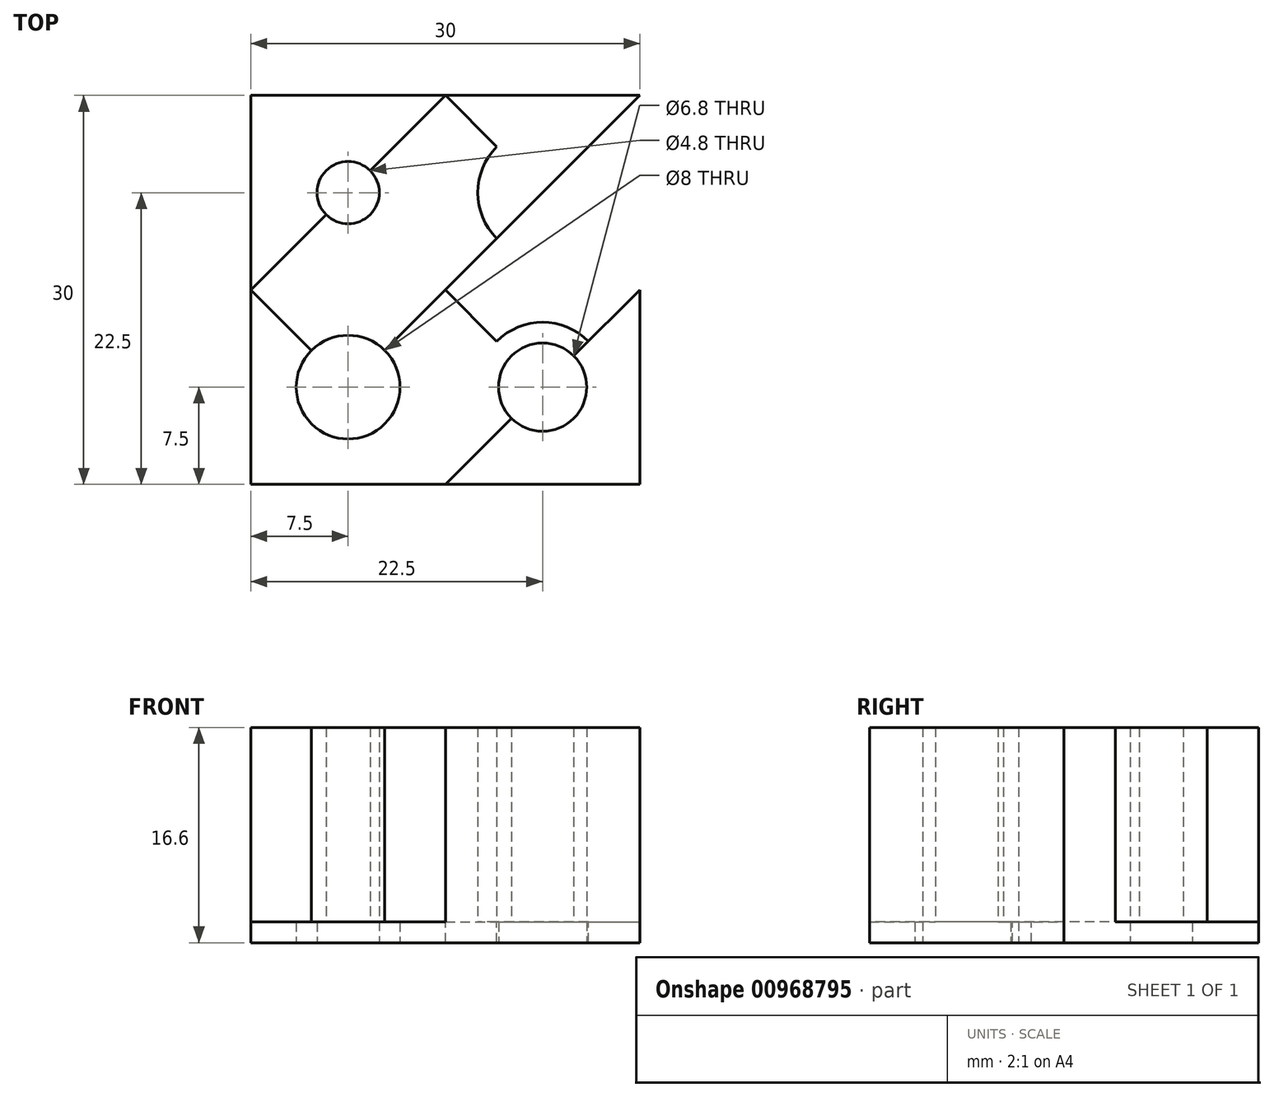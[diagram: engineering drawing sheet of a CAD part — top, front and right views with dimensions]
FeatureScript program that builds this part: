
annotation { "Feature Type Name" : "Feature", "Feature Type Description" : "" }
export const myFeature = defineFeature(function(context is Context, id is Id, definition is map)
    precondition{}
    {
        {
            var Q0;
            Q0=qCreatedBy(makeId("Top.planeOp"),FACE);
            var sketch = newSketch(context, id + "F0", { "sketchPlane" : qUnion([Q0])});
            skLineSegment(sketch, "E0.bottom", {"start": v(0, 0) * mm, "end": v(30, 0) * mm});
            skLineSegment(sketch, "E0.top", {"start": v(0, -30) * mm, "end": v(30, -30) * mm});
            skLineSegment(sketch, "E0.left", {"start": v(0, 0) * mm, "end": v(0, -30) * mm});
            skLineSegment(sketch, "E0.right", {"start": v(30, 0) * mm, "end": v(30, -30) * mm});
            skSolve(sketch);
        }
        {
            var Q0;
            Q0=makeQuery(id+"F0.imprint","IMPRINT",FACE,{"disambiguationData":[TD([[makeQuery(id+"F0.imprint","IMPRINT",EDGE,{"derivedFrom":sQuery(id+"F0.wireOp",EDGE,"E0.bottom")}),-1.0]])]});
            extrude(context, id + "F1", {"entities" : qUnion([Q0]), "depth" : 1.6 * mm, "offsetDistance" : 25 * mm});
        }
        {
            var Q0;
            Q0=makeQuery(id+"F1.opExtrude","CAP_FACE",FACE,{"disambiguationData":[OSD([sQuery(id+"F0.wireOp",EDGE,"E0.bottom"),sQuery(id+"F0.wireOp",EDGE,"E0.top"),sQuery(id+"F0.wireOp",EDGE,"E0.left"),sQuery(id+"F0.wireOp",EDGE,"E0.right")])],"isStart":false});
            var sketch = newSketch(context, id + "F2", { "sketchPlane" : qUnion([Q0])});
            skLineSegment(sketch, "E1", {"start": v(0, 0) * mm, "end": v(30, -30) * mm});
            skLineSegment(sketch, "E2", {"start": v(15, -30) * mm, "end": v(30, -15) * mm});
            skLineSegment(sketch, "E3", {"start": v(15, 0) * mm, "end": v(0, -15) * mm});
            skCircle(sketch, "E4", {"center": v(7.5, -7.5) * mm, "radius": 4 * mm});
            skCircle(sketch, "E5", {"center": v(22.5, -22.5) * mm, "radius": 5 * mm});
            skCircle(sketch, "E6.0", {"center": v(7.5, -7.5) * mm, "radius": 2.4 * mm});
            skLineSegment(sketch, "E7", {"start": v(15, 0) * mm, "end": v(30, -15) * mm});
            skLineSegment(sketch, "E8", {"start": v(0, -15) * mm, "end": v(15, -30) * mm});
            skLineSegment(sketch, "E9", {"start": v(0, -30) * mm, "end": v(30, 0) * mm});
            skCircle(sketch, "E10", {"center": v(22.5, -7.5) * mm, "radius": 5 * mm});
            skCircle(sketch, "E11", {"center": v(7.5, -22.5) * mm, "radius": 4 * mm});
            skCircle(sketch, "E12", {"center": v(22.5, -22.5) * mm, "radius": 3.4 * mm});
            skSolve(sketch);
        }
        {
            var Q0;
            {var subQ0=sQuery(id+"F2.wireOp",EDGE,"E4");var subQ1=sQuery(id+"F2.wireOp",EDGE,"E1");var subQ2=makeQuery(id+"F2.imprint","INTERSECT",VERTEX,{"disambiguationData":[OD(0.0)],"derivedFrom":[subQ1,subQ0]});Q0=makeQuery(id+"F2.imprint","IMPRINT",FACE,{"disambiguationData":[TD([[makeQuery(id+"F2.imprint","IMPRINT",EDGE,{"disambiguationData":[TD([[subQ2,-1.0]])],"derivedFrom":subQ1}),-1.0]])]});}
            var Q1;
            {var subQ0=sQuery(id+"F2.wireOp",EDGE,"E4");var subQ1=sQuery(id+"F2.wireOp",EDGE,"E1");var subQ2=makeQuery(id+"F2.imprint","INTERSECT",VERTEX,{"disambiguationData":[OD(0.0)],"derivedFrom":[subQ1,subQ0]});Q1=makeQuery(id+"F2.imprint","IMPRINT",FACE,{"disambiguationData":[TD([[makeQuery(id+"F2.imprint","IMPRINT",EDGE,{"disambiguationData":[TD([[subQ2,-1.0]])],"derivedFrom":subQ1}),1.0]])]});}
            var Q2;
            {var subQ0=sQuery(id+"F2.wireOp",EDGE,"E6.0");var subQ1=sQuery(id+"F2.wireOp",EDGE,"E1");var subQ2=makeQuery(id+"F2.imprint","INTERSECT",VERTEX,{"disambiguationData":[OD(1.0)],"derivedFrom":[subQ1,subQ0]});Q2=makeQuery(id+"F2.imprint","IMPRINT",FACE,{"disambiguationData":[TD([[makeQuery(id+"F2.imprint","IMPRINT",EDGE,{"disambiguationData":[TD([[subQ2,-1.0]])],"derivedFrom":subQ1}),1.0]])]});}
            var Q3;
            {var subQ0=sQuery(id+"F2.wireOp",EDGE,"E6.0");var subQ1=sQuery(id+"F2.wireOp",EDGE,"E1");var subQ2=makeQuery(id+"F2.imprint","INTERSECT",VERTEX,{"disambiguationData":[OD(1.0)],"derivedFrom":[subQ1,subQ0]});Q3=makeQuery(id+"F2.imprint","IMPRINT",FACE,{"disambiguationData":[TD([[makeQuery(id+"F2.imprint","IMPRINT",EDGE,{"disambiguationData":[TD([[subQ2,-1.0]])],"derivedFrom":subQ1}),-1.0]])]});}
            var Q4;
            {var subQ0=sQuery(id+"F2.wireOp",EDGE,"E5");var subQ1=sQuery(id+"F2.wireOp",EDGE,"E1");var subQ2=makeQuery(id+"F2.imprint","INTERSECT",VERTEX,{"disambiguationData":[OD(0.0)],"derivedFrom":[subQ1,subQ0]});Q4=makeQuery(id+"F2.imprint","IMPRINT",FACE,{"disambiguationData":[TD([[makeQuery(id+"F2.imprint","IMPRINT",EDGE,{"disambiguationData":[TD([[subQ2,-1.0]])],"derivedFrom":subQ1}),-1.0]])]});}
            var Q5;
            {var subQ0=sQuery(id+"F2.wireOp",EDGE,"E5");var subQ1=sQuery(id+"F2.wireOp",EDGE,"E1");var subQ2=makeQuery(id+"F2.imprint","INTERSECT",VERTEX,{"disambiguationData":[OD(0.0)],"derivedFrom":[subQ1,subQ0]});Q5=makeQuery(id+"F2.imprint","IMPRINT",FACE,{"disambiguationData":[TD([[makeQuery(id+"F2.imprint","IMPRINT",EDGE,{"disambiguationData":[TD([[subQ2,-1.0]])],"derivedFrom":subQ1}),1.0]])]});}
            var Q6;
            {var subQ0=sQuery(id+"F2.wireOp",EDGE,"E12");var subQ1=sQuery(id+"F2.wireOp",EDGE,"E1");var subQ2=makeQuery(id+"F2.imprint","INTERSECT",VERTEX,{"disambiguationData":[OD(1.0)],"derivedFrom":[subQ1,subQ0]});Q6=makeQuery(id+"F2.imprint","IMPRINT",FACE,{"disambiguationData":[TD([[makeQuery(id+"F2.imprint","IMPRINT",EDGE,{"disambiguationData":[TD([[subQ2,-1.0]])],"derivedFrom":subQ1}),1.0]])]});}
            var Q7;
            {var subQ0=sQuery(id+"F2.wireOp",EDGE,"E12");var subQ1=sQuery(id+"F2.wireOp",EDGE,"E1");var subQ2=makeQuery(id+"F2.imprint","INTERSECT",VERTEX,{"disambiguationData":[OD(1.0)],"derivedFrom":[subQ1,subQ0]});Q7=makeQuery(id+"F2.imprint","IMPRINT",FACE,{"disambiguationData":[TD([[makeQuery(id+"F2.imprint","IMPRINT",EDGE,{"disambiguationData":[TD([[subQ2,-1.0]])],"derivedFrom":subQ1}),-1.0]])]});}
            extrude(context, id + "F3", {"entities" : qUnion([Q0, Q1, Q2, Q3, Q4, Q5, Q6, Q7]), "operationType" : NewBodyOperationType.ADD, "depth" : 15 * mm, "offsetDistance" : 25 * mm});
        }
        {
            var Q0;
            {var subQ0=sQuery(id+"F2.wireOp",EDGE,"E9");var subQ1=sQuery(id+"F2.wireOp",EDGE,"E7");var subQ2=makeQuery(id+"F2.imprint","INTERSECT",VERTEX,{"derivedFrom":[subQ1,subQ0]});Q0=makeQuery(id+"F2.imprint","IMPRINT",FACE,{"disambiguationData":[TD([[makeQuery(id+"F2.imprint","IMPRINT",EDGE,{"disambiguationData":[TD([[subQ2,-1.0]])],"derivedFrom":subQ1}),-1.0]])]});}
            var Q1;
            {var subQ0=sQuery(id+"F2.wireOp",EDGE,"E10");var subQ1=sQuery(id+"F2.wireOp",EDGE,"E7");var subQ2=makeQuery(id+"F2.imprint","INTERSECT",VERTEX,{"disambiguationData":[OD(0.0)],"derivedFrom":[subQ1,subQ0]});Q1=makeQuery(id+"F2.imprint","IMPRINT",FACE,{"disambiguationData":[TD([[makeQuery(id+"F2.imprint","IMPRINT",EDGE,{"disambiguationData":[TD([[subQ2,-1.0]])],"derivedFrom":subQ1}),-1.0]])]});}
            var Q2;
            {var subQ0=sQuery(id+"F2.wireOp",EDGE,"E10");var subQ1=sQuery(id+"F2.wireOp",EDGE,"E7");var subQ2=makeQuery(id+"F2.imprint","INTERSECT",VERTEX,{"disambiguationData":[OD(0.0)],"derivedFrom":[subQ1,subQ0]});Q2=makeQuery(id+"F2.imprint","IMPRINT",FACE,{"disambiguationData":[TD([[makeQuery(id+"F2.imprint","IMPRINT",EDGE,{"disambiguationData":[TD([[subQ2,-1.0]])],"derivedFrom":subQ1}),1.0]])]});}
            var Q3;
            {var subQ0=sQuery(id+"F2.wireOp",EDGE,"E9");var subQ1=sQuery(id+"F2.wireOp",EDGE,"E7");var subQ2=makeQuery(id+"F2.imprint","INTERSECT",VERTEX,{"derivedFrom":[subQ1,subQ0]});Q3=makeQuery(id+"F2.imprint","IMPRINT",FACE,{"disambiguationData":[TD([[makeQuery(id+"F2.imprint","IMPRINT",EDGE,{"disambiguationData":[TD([[subQ2,-1.0]])],"derivedFrom":subQ1}),1.0]])]});}
            var Q4;
            {var subQ0=sQuery(id+"F2.wireOp",EDGE,"E3");var subQ1=sQuery(id+"F2.wireOp",EDGE,"E1");var subQ2=makeQuery(id+"F2.imprint","INTERSECT",VERTEX,{"derivedFrom":[subQ1,subQ0]});Q4=makeQuery(id+"F2.imprint","IMPRINT",FACE,{"disambiguationData":[TD([[makeQuery(id+"F2.imprint","IMPRINT",EDGE,{"disambiguationData":[TD([[subQ2,-1.0]])],"derivedFrom":subQ1}),1.0]])]});}
            var Q5;
            {var subQ0=sQuery(id+"F2.wireOp",EDGE,"E6.0");var subQ1=sQuery(id+"F2.wireOp",EDGE,"E1");var subQ2=makeQuery(id+"F2.imprint","INTERSECT",VERTEX,{"disambiguationData":[OD(0.0)],"derivedFrom":[subQ1,subQ0]});Q5=makeQuery(id+"F2.imprint","IMPRINT",FACE,{"disambiguationData":[TD([[makeQuery(id+"F2.imprint","IMPRINT",EDGE,{"disambiguationData":[TD([[subQ2,-1.0]])],"derivedFrom":subQ1}),1.0]])]});}
            var Q6;
            {var subQ0=sQuery(id+"F2.wireOp",EDGE,"E6.0");var subQ1=sQuery(id+"F2.wireOp",EDGE,"E1");var subQ2=makeQuery(id+"F2.imprint","INTERSECT",VERTEX,{"disambiguationData":[OD(0.0)],"derivedFrom":[subQ1,subQ0]});Q6=makeQuery(id+"F2.imprint","IMPRINT",FACE,{"disambiguationData":[TD([[makeQuery(id+"F2.imprint","IMPRINT",EDGE,{"disambiguationData":[TD([[subQ2,-1.0]])],"derivedFrom":subQ1}),-1.0]])]});}
            var Q7;
            {var subQ0=sQuery(id+"F2.wireOp",EDGE,"E3");var subQ1=sQuery(id+"F2.wireOp",EDGE,"E1");var subQ2=makeQuery(id+"F2.imprint","INTERSECT",VERTEX,{"derivedFrom":[subQ1,subQ0]});Q7=makeQuery(id+"F2.imprint","IMPRINT",FACE,{"disambiguationData":[TD([[makeQuery(id+"F2.imprint","IMPRINT",EDGE,{"disambiguationData":[TD([[subQ2,-1.0]])],"derivedFrom":subQ1}),-1.0]])]});}
            var Q8;
            {var subQ0=sQuery(id+"F2.wireOp",EDGE,"E11");var subQ1=sQuery(id+"F2.wireOp",EDGE,"E8");var subQ2=makeQuery(id+"F2.imprint","INTERSECT",VERTEX,{"disambiguationData":[OD(0.0)],"derivedFrom":[subQ1,subQ0]});Q8=makeQuery(id+"F2.imprint","IMPRINT",FACE,{"disambiguationData":[TD([[makeQuery(id+"F2.imprint","IMPRINT",EDGE,{"disambiguationData":[TD([[subQ2,-1.0]])],"derivedFrom":subQ1}),1.0]])]});}
            var Q9;
            {var subQ0=sQuery(id+"F2.wireOp",EDGE,"E9");var subQ1=sQuery(id+"F2.wireOp",EDGE,"E8");var subQ2=makeQuery(id+"F2.imprint","INTERSECT",VERTEX,{"derivedFrom":[subQ1,subQ0]});Q9=makeQuery(id+"F2.imprint","IMPRINT",FACE,{"disambiguationData":[TD([[makeQuery(id+"F2.imprint","IMPRINT",EDGE,{"disambiguationData":[TD([[subQ2,-1.0]])],"derivedFrom":subQ1}),1.0]])]});}
            var Q10;
            {var subQ0=sQuery(id+"F2.wireOp",EDGE,"E9");var subQ1=sQuery(id+"F2.wireOp",EDGE,"E8");var subQ2=makeQuery(id+"F2.imprint","INTERSECT",VERTEX,{"derivedFrom":[subQ1,subQ0]});Q10=makeQuery(id+"F2.imprint","IMPRINT",FACE,{"disambiguationData":[TD([[makeQuery(id+"F2.imprint","IMPRINT",EDGE,{"disambiguationData":[TD([[subQ2,-1.0]])],"derivedFrom":subQ1}),-1.0]])]});}
            var Q11;
            {var subQ0=sQuery(id+"F2.wireOp",EDGE,"E11");var subQ1=sQuery(id+"F2.wireOp",EDGE,"E8");var subQ2=makeQuery(id+"F2.imprint","INTERSECT",VERTEX,{"disambiguationData":[OD(0.0)],"derivedFrom":[subQ1,subQ0]});Q11=makeQuery(id+"F2.imprint","IMPRINT",FACE,{"disambiguationData":[TD([[makeQuery(id+"F2.imprint","IMPRINT",EDGE,{"disambiguationData":[TD([[subQ2,-1.0]])],"derivedFrom":subQ1}),-1.0]])]});}
            var Q12;
            {var subQ0=sQuery(id+"F2.wireOp",EDGE,"E12");var subQ1=sQuery(id+"F2.wireOp",EDGE,"E1");var subQ2=makeQuery(id+"F2.imprint","INTERSECT",VERTEX,{"disambiguationData":[OD(0.0)],"derivedFrom":[subQ1,subQ0]});Q12=makeQuery(id+"F2.imprint","IMPRINT",FACE,{"disambiguationData":[TD([[makeQuery(id+"F2.imprint","IMPRINT",EDGE,{"disambiguationData":[TD([[subQ2,-1.0]])],"derivedFrom":subQ1}),-1.0]])]});}
            var Q13;
            {var subQ0=sQuery(id+"F2.wireOp",EDGE,"E12");var subQ1=sQuery(id+"F2.wireOp",EDGE,"E1");var subQ2=makeQuery(id+"F2.imprint","INTERSECT",VERTEX,{"disambiguationData":[OD(0.0)],"derivedFrom":[subQ1,subQ0]});Q13=makeQuery(id+"F2.imprint","IMPRINT",FACE,{"disambiguationData":[TD([[makeQuery(id+"F2.imprint","IMPRINT",EDGE,{"disambiguationData":[TD([[subQ2,-1.0]])],"derivedFrom":subQ1}),1.0]])]});}
            var Q14;
            {var subQ0=sQuery(id+"F2.wireOp",EDGE,"E2");var subQ1=sQuery(id+"F2.wireOp",EDGE,"E1");var subQ2=makeQuery(id+"F2.imprint","INTERSECT",VERTEX,{"derivedFrom":[subQ1,subQ0]});Q14=makeQuery(id+"F2.imprint","IMPRINT",FACE,{"disambiguationData":[TD([[makeQuery(id+"F2.imprint","IMPRINT",EDGE,{"disambiguationData":[TD([[subQ2,-1.0]])],"derivedFrom":subQ1}),1.0]])]});}
            var Q15;
            {var subQ0=sQuery(id+"F2.wireOp",EDGE,"E2");var subQ1=sQuery(id+"F2.wireOp",EDGE,"E1");var subQ2=makeQuery(id+"F2.imprint","INTERSECT",VERTEX,{"derivedFrom":[subQ1,subQ0]});Q15=makeQuery(id+"F2.imprint","IMPRINT",FACE,{"disambiguationData":[TD([[makeQuery(id+"F2.imprint","IMPRINT",EDGE,{"disambiguationData":[TD([[subQ2,-1.0]])],"derivedFrom":subQ1}),-1.0]])]});}
            extrude(context, id + "F4", {"entities" : qUnion([Q0, Q1, Q2, Q3, Q4, Q5, Q6, Q7, Q8, Q9, Q10, Q11, Q12, Q13, Q14, Q15]), "operationType" : NewBodyOperationType.REMOVE, "oppositeDirection" : true, "depth" : 25 * mm, "offsetDistance" : 25 * mm});
        }
    });
